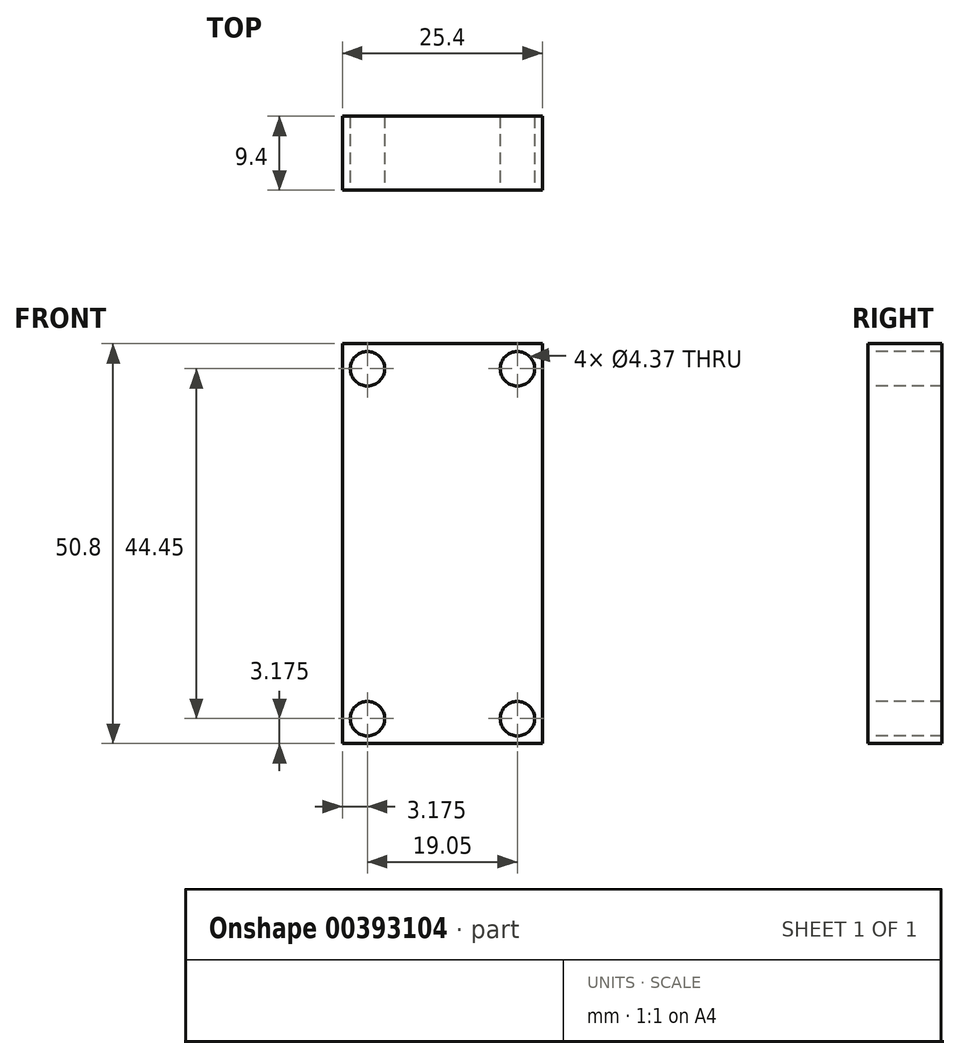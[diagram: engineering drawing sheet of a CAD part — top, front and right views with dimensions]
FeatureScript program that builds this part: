
annotation { "Feature Type Name" : "Feature", "Feature Type Description" : "" }
export const myFeature = defineFeature(function(context is Context, id is Id, definition is map)
    precondition{}
    {
        {
            var Q0;
            Q0=qCreatedBy(makeId("Front.planeOp"),FACE);
            var sketch = newSketch(context, id + "F0", { "sketchPlane" : qUnion([Q0])});
            skLineSegment(sketch, "E0.bottom", {"start": v(12.7, 25.4) * mm, "end": v(-12.7, 25.4) * mm});
            skLineSegment(sketch, "E0.top", {"start": v(12.7, -25.4) * mm, "end": v(-12.7, -25.4) * mm});
            skLineSegment(sketch, "E0.left", {"start": v(12.7, 25.4) * mm, "end": v(12.7, -25.4) * mm});
            skLineSegment(sketch, "E0.right", {"start": v(-12.7, 25.4) * mm, "end": v(-12.7, -25.4) * mm});
            skPoint(sketch, "E0.middle", {"position": v(0, 0) * mm});
            skPoint(sketch, "E1", {"position": v(-9.53, 22.22) * mm});
            skPoint(sketch, "E2", {"position": v(9.52, 22.22) * mm});
            skPoint(sketch, "E3", {"position": v(-9.53, -22.23) * mm});
            skPoint(sketch, "E4", {"position": v(9.53, -22.23) * mm});
            skSolve(sketch);
        }
        {
            var Q0;
            Q0=makeQuery(id+"F0.imprint","IMPRINT",FACE,{"disambiguationData":[TD([[makeQuery(id+"F0.imprint","IMPRINT",EDGE,{"derivedFrom":sQuery(id+"F0.wireOp",EDGE,"E0.bottom")}),1.0]])]});
            extrude(context, id + "F1", {"entities" : qUnion([Q0]), "oppositeDirection" : true, "depth" : 9.4 * mm});
        }
        {
            var Q0;
            Q0=sQuery(id+"F0.wireOp",VERTEX,"E1");
            var Q1;
            Q1=sQuery(id+"F0.wireOp",VERTEX,"E2");
            var Q2;
            Q2=sQuery(id+"F0.wireOp",VERTEX,"E4");
            var Q3;
            Q3=sQuery(id+"F0.wireOp",VERTEX,"E3");
            var Q4;
            Q4=makeQuery(id+"F1.opExtrude","SWEPT_BODY",BODY,{"disambiguationData":[OSD([sQuery(id+"F0.wireOp",EDGE,"E0.bottom"),sQuery(id+"F0.wireOp",EDGE,"E0.top"),sQuery(id+"F0.wireOp",EDGE,"E0.left"),sQuery(id+"F0.wireOp",EDGE,"E0.right")])]});
            hole(context, id + "F2", {"style" : HoleStyle.SIMPLE, "endStyle" : HoleEndStyle.THROUGH, "holeDiameter" : 4.37 * mm, "isTappedThrough" : true, "tappedDepth" : 6.35 * mm, "tapClearance" : 3, "locations" : qUnion([Q0, Q1, Q2, Q3]), "scope" : qUnion([Q4])});
        }
    });
